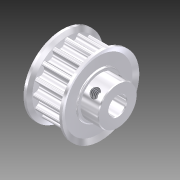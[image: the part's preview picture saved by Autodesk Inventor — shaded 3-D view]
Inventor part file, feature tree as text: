
AUTODESK INVENTOR PART (.ipt)
format: ipt  version: 2011 (Build 150239000, 239)  size: 481,280 bytes
history: native  units: mm
features: thread x2, imported_body x1
ambient origin geometry x8: Origin, YZ Plane, XZ Plane, XY Plane, X Axis, Y Axis, Z Axis, Center Point
bodies: Solid1 (feature_tree)
feature tree (3):
  imported_body  "Base1"
  thread  "Thread1"  [1 undecoded]
  thread  "Thread2"  [1 undecoded]
note: 2 required parameter values undecoded (feature->parameter linkage not recoverable at this tier; creation-order binding heuristic only, values carry confidence <= 0.55)
